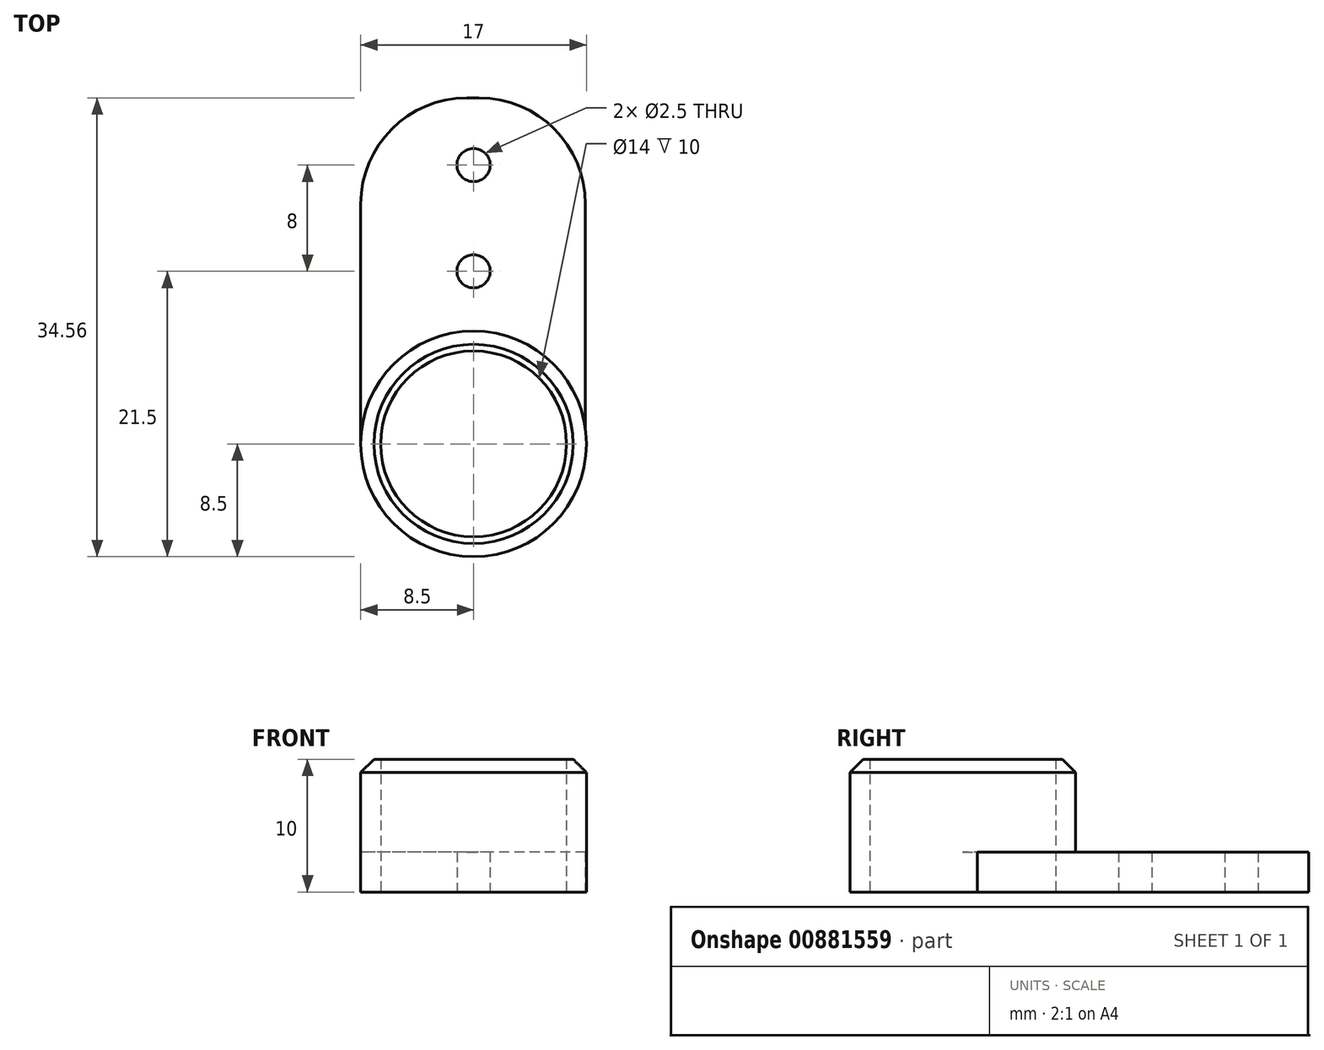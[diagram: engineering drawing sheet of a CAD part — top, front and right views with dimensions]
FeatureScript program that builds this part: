
annotation { "Feature Type Name" : "Feature", "Feature Type Description" : "" }
export const myFeature = defineFeature(function(context is Context, id is Id, definition is map)
    precondition{}
    {
        {
            var Q0;
            Q0=qCreatedBy(makeId("Top.planeOp"),FACE);
            var sketch = newSketch(context, id + "F0", { "sketchPlane" : qUnion([Q0])});
            skCircle(sketch, "E0", {"center": v(0, 0) * mm, "radius": 8.5 * mm});
            skLineSegment(sketch, "E1.bottom", {"start": v(-8.5, 0) * mm, "end": v(8.43, 0) * mm});
            skLineSegment(sketch, "E1.top", {"start": v(-8.5, 26.06) * mm, "end": v(8.43, 26.06) * mm});
            skLineSegment(sketch, "E1.left", {"start": v(-8.5, 0) * mm, "end": v(-8.5, 26.06) * mm});
            skLineSegment(sketch, "E1.right", {"start": v(8.43, 0) * mm, "end": v(8.43, 26.06) * mm});
            skPoint(sketch, "E2", {"position": v(0, 21) * mm});
            skPoint(sketch, "E3", {"position": v(0, 13) * mm});
            skSolve(sketch);
        }
        {
            var Q0;
            {var subQ0=sQuery(id+"F0.wireOp",EDGE,"E1.bottom");Q0=makeQuery(id+"F0.imprint","IMPRINT",FACE,{"disambiguationData":[TD([[makeQuery(id+"F0.imprint","IMPRINT",EDGE,{"derivedFrom":subQ0}),1.0]])]});}
            var Q1;
            {var subQ0=sQuery(id+"F0.wireOp",EDGE,"E1.bottom");Q1=makeQuery(id+"F0.imprint","IMPRINT",FACE,{"disambiguationData":[TD([[makeQuery(id+"F0.imprint","IMPRINT",EDGE,{"derivedFrom":subQ0}),-1.0]])]});}
            extrude(context, id + "F1", {"entities" : qUnion([Q0, Q1]), "depth" : 10 * mm, "offsetDistance" : 25 * mm});
        }
        {
            var Q0;
            {var subQ4=sQuery(id+"F0.wireOp",EDGE,"E1.top");Q0=makeQuery(id+"F0.imprint","IMPRINT",FACE,{"disambiguationData":[TD([[makeQuery(id+"F0.imprint","IMPRINT",EDGE,{"derivedFrom":subQ4}),-1.0]])]});}
            extrude(context, id + "F2", {"entities" : qUnion([Q0]), "operationType" : NewBodyOperationType.ADD, "depth" : 3 * mm, "offsetDistance" : 25 * mm});
        }
        {
            var Q0;
            Q0=makeQuery(id+"F2.opExtrude","SWEPT_EDGE",EDGE,{"disambiguationData":[OSD([sQuery(id+"F0.wireOp",EDGE,"E1.top"),sQuery(id+"F0.wireOp",EDGE,"E1.left")])]});
            var Q1;
            Q1=makeQuery(id+"F2.opExtrude","SWEPT_EDGE",EDGE,{"disambiguationData":[OSD([sQuery(id+"F0.wireOp",EDGE,"E1.top"),sQuery(id+"F0.wireOp",EDGE,"E1.right")])]});
            fillet(context, id + "F3", {"entities" : qUnion([Q0, Q1]), "radius" : 8 * mm, "tangentPropagation" : true, "allowEdgeOverflow" : false});
        }
        {
            var Q0;
            Q0=sQuery(id+"F0.wireOp",VERTEX,"E0.center");
            var Q1;
            Q1=makeQuery(id+"F1.opExtrude","SWEPT_BODY",BODY,{"disambiguationData":[OSD([sQuery(id+"F0.wireOp",EDGE,"E0")])]});
            hole(context, id + "F4", {"style" : HoleStyle.SIMPLE, "endStyle" : HoleEndStyle.THROUGH, "oppositeDirection" : true, "holeDiameter" : 14 * mm, "majorDiameter" : 5 * mm, "isTappedThrough" : true, "tappedDepth" : 12 * mm, "tapClearance" : 3, "startFromSketch" : true, "locations" : qUnion([Q0]), "scope" : qUnion([Q1])});
        }
        {
            var Q0;
            Q0=makeQuery(id+"F1.opExtrude","CAP_EDGE",EDGE,{"disambiguationData":[OSD([sQuery(id+"F0.wireOp",EDGE,"E0")])],"isStart":false});
            chamfer(context, id + "F5", {"entities" : qUnion([Q0]), "width" : 1 * mm, "tangentPropagation" : true});
        }
        {
            var Q0;
            Q0=sQuery(id+"F0.wireOp",VERTEX,"E2");
            var Q1;
            Q1=sQuery(id+"F0.wireOp",VERTEX,"E3");
            var Q2;
            Q2=makeQuery(id+"F1.opExtrude","SWEPT_BODY",BODY,{"disambiguationData":[OSD([sQuery(id+"F0.wireOp",EDGE,"E0")])]});
            hole(context, id + "F6", {"style" : HoleStyle.SIMPLE, "endStyle" : HoleEndStyle.THROUGH, "oppositeDirection" : true, "holeDiameter" : 2.5 * mm, "majorDiameter" : 5 * mm, "isTappedThrough" : true, "tappedDepth" : 12 * mm, "tapClearance" : 3, "startFromSketch" : true, "locations" : qUnion([Q0, Q1]), "scope" : qUnion([Q2])});
        }
    });
